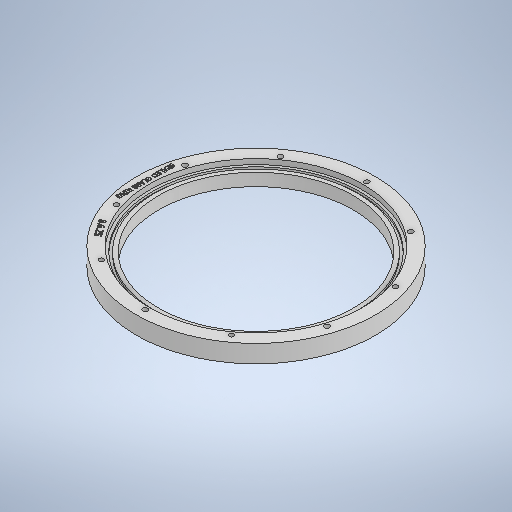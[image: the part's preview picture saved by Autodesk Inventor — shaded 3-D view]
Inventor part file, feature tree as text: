
AUTODESK INVENTOR PART (.ipt)
format: ipt  version: 2025 (Build 290162000, 162)  size: 789,504 bytes
history: native  units: mm
features: sketch x6, extrude x3, emboss x2, hole x1, pattern_circular x1
ambient origin geometry x8: Origin, YZ Plane, XZ Plane, XY Plane, X Axis, Y Axis, Z Axis, Center Point
bodies: Solid1 (feature_tree)
feature tree (13):
  extrude  "Ring"  Depth=270.0mm
  extrude  "Glass Seat"  Depth=241.0mm
  hole  "Holes"  [1 undecoded]
  pattern_circular  "Circular Pattern1"  Count=10 Angle=360.0deg
  emboss  "Emboss1"
  extrude  "Seal Groove"  Depth=2.5mm TaperAngle=0.0deg
  emboss  "Emboss2"
  sketch  "Sketch1"  dims[d0=220.0mm d1=270.0mm]
  sketch  "Sketch2"  dims[d2=20.0mm d3=0.0mm d4=241.0mm]
  sketch  "Sketch3"  dims[d5=5.9mm d6=0.0mm]
  sketch  "Sketch4"  dims[d7=5.5mm d8=6.0mm d9=4.0mm d10=2.0mm d11=90.0deg d12=8.0mm d13=20.594885mm d14=125.0mm d15=100.0mm d16=360.0deg]
  sketch  "Sketch5"  dims[d18=1.0mm d19=0.0mm d23=2.5mm d24=0.0mm]
  sketch  "Sketch6"  dims[d25=3.0mm d26=3.0mm d27=1.0mm d28=0.0mm]
note: 1 required parameter value undecoded (feature->parameter linkage not recoverable at this tier; creation-order binding heuristic only, values carry confidence <= 0.55)
